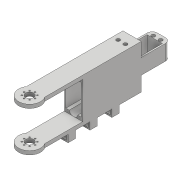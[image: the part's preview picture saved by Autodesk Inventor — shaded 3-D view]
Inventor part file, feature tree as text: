
AUTODESK INVENTOR PART (.ipt)
format: ipt  version: 2018 (Build 220112000, 112)  size: 361,984 bytes
history: native  units: mm
features: extrude x12, sketch x11, move_body x10, direct_edit x2, fillet x1
ambient origin geometry x8: Origin, YZ Plane, XZ Plane, XY Plane, X Axis, Y Axis, Z Axis, Center Point
bodies: Solid1 (feature_tree)
feature tree (36):
  extrude  "base"  Depth=190.0mm
  extrude  "shape_base"  Depth=5.0mm
  extrude  "internal_servo_slot"  Depth=50.0mm
  extrude  "shape_end"  Depth=60.0mm
  extrude  "servo_attach_end"  Depth=10.0mm
  sketch  "Sketch6"  dims[d12=10.0mm d13=12.0mm d14=12.0mm]
  extrude  "servo_attach_base"  Depth=10.0mm
  fillet  "Fillet1"  Radius=12.0mm
  extrude  "Extrusion7"  Depth=40.0mm
  extrude  "Extrusion8"  Depth=19.0mm
  extrude  "Extrusion9"  Depth=40.0mm
  extrude  "Extrusion10"  Depth=6.0mm
  extrude  "Extrusion11"  Depth=5.0mm
  extrude  "Extrusion12"  Depth=6.0mm
  direct_edit  "Direct Edit1"
  direct_edit  "Direct Edit2"
  sketch  "Sketch1"  dims[d0=24.0mm d1=190.0mm]
  sketch  "Sketch2"  dims[d2=60.0mm d3=0.0mm d4=5.0mm]
  sketch  "Sketch3"  dims[d5=70.0mm d6=50.0mm]
  sketch  "Sketch4"  dims[d7=60.0mm d8=0.0mm d9=19.5mm]
  sketch  "Sketch5"  dims[d10=39.0mm d11=10.0mm]
  sketch  "Sketch7"  dims[d15=111.0mm d16=0.0mm d17=40.0mm]
  sketch  "Sketch8"  dims[d18=40.0mm d19=19.0mm]
  sketch  "Sketch9"  dims[d20=20.0mm d21=40.0mm]
  sketch  "Sketch10"  dims[d22=60.0mm d23=0.0mm d24=6.0mm]
  sketch  "Sketch11"  dims[d25=7.0mm d26=5.0mm d27=6.0mm d28=7.0mm d29=5.0mm d30=60.0mm d31=0.0mm d32=10.0mm d33=11.0mm d34=7.5mm d35=2.0mm d36=80.0mm d38=360.0deg d40=60.0mm d41=0.0mm d42=7.0mm d43=50.1mm d44=10.0mm d45=180.0deg d46=5.0mm d47=5.0mm d48=60.0mm d49=0.0mm d50=30.0mm d51=10.0mm d52=20.0mm d53=10.0mm d54=20.0mm d55=10.0mm d56=10.0mm d57=0.0mm d58=2.0mm d59=8.0mm d60=20.0mm d61=10.0mm d62=0.0mm d63=30.0mm d64=10.0mm d65=0.0mm d66=30.0mm d67=10.0mm d68=0.0mm d69=10.0mm d70=0.0mm d72=0.0mm d73=0.0mm d74=-1.0mm d75=0.0mm d76=0.0mm d77=-1.0mm d78=0.0mm d79=0.0mm d80=-0.5mm d81=0.0mm d82=0.0mm d83=-0.5mm d84=0.0mm d85=0.0mm d86=0.5mm d87=0.0mm d88=0.0mm d89=0.5mm d90=0.0mm d91=2.0mm d92=0.0mm d93=0.0mm d94=2.0mm d95=0.0mm d96=0.0mm d97=-2.0mm d98=0.0mm d99=0.0mm d100=-2.0mm d101=0.0mm]
  move_body  "Move1"
  move_body  "Move2"
  move_body  "Move3"
  move_body  "Move4"
  move_body  "Move5"
  move_body  "Move6"
  move_body  "Move7"
  move_body  "Move8"
  move_body  "Move9"
  move_body  "Move10"
